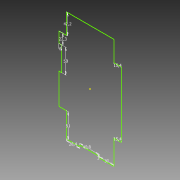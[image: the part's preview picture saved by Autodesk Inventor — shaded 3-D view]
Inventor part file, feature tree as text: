
AUTODESK INVENTOR PART (.ipt)
format: ipt  version: 2015 (Build 190159000, 159)  size: 73,216 bytes
history: native  units: mm
features: sketch x1
ambient origin geometry x8: Origin, YZ Plane, XZ Plane, XY Plane, X Axis, Y Axis, Z Axis, Center Point
feature tree (1):
  sketch  "Sketch1"  dims[d3=51.0mm d5=15.4mm d8=15.4mm d10=42.2mm d11=28.4mm d13=30.0mm d14=3.0mm d15=40.8mm d16=22.3mm d17=6.0mm d18=50.0mm]
